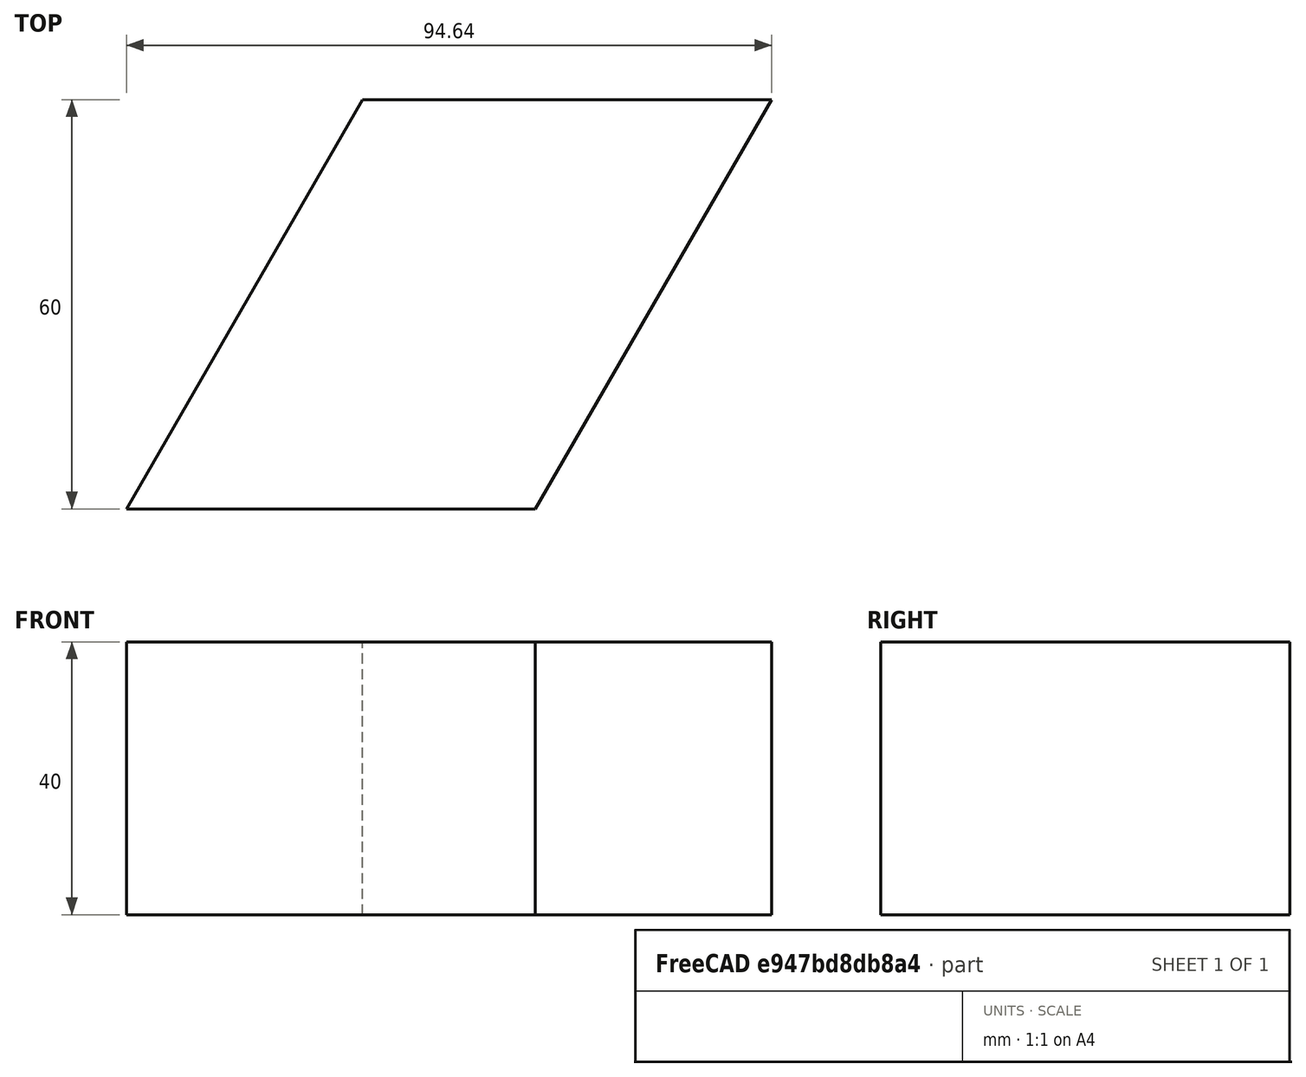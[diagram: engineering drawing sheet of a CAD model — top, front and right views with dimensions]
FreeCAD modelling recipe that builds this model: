
FCSTD DOCUMENT  (FreeCAD 0.19R)
Label: Rhombus
License: All rights reserved
LicenseURL: http://en.wikipedia.org/wiki/All_rights_reserved
objects: Sketcher::SketchObject×1, PartDesign::Pad×1, PartDesign::Body×1
note: 4 computed .brp shape members not serialized (recipe doc carries the construction recipe); baked Part::Feature solids carry a one-line shape summary decoded from their .brp

FEATURE [Sketcher::SketchObject] Sketch
  FullyConstrained = true
  MapMode = 5
  Support = -> [XY_Plane]
  sketch-geometry (4):
    g0: LineSegment StartX=57.631 StartY=83.67 StartZ=0 EndX=117.631 EndY=83.67 EndZ=0
    g1: LineSegment StartX=117.631 StartY=83.67 StartZ=0 EndX=82.99 EndY=23.67 EndZ=0
    g2: LineSegment StartX=82.99 StartY=23.67 StartZ=0 EndX=22.99 EndY=23.67 EndZ=0
    g3: LineSegment StartX=22.99 StartY=23.67 StartZ=0 EndX=57.631 EndY=83.67 EndZ=0
  constraints (12):
    c: Coincident(g0,g1)
    c: Coincident(g1,g2)
    c: Coincident(g2,g3)
    c: Coincident(g3,g0)
    c: Horizontal(g0)
    c: Horizontal(g2)
    c: DistanceX(g-1,g2) = 22.99
    c: DistanceY(g-1,g2) = 23.67
    c: DistanceX(g2,g1) = 60
    c: DistanceY(g1,g1) = 60
    c: Equal(g0,g2)
    c: Angle(g2,g3) = 1.0472
FEATURE [PartDesign::Pad] Pad
  Direction = (1,1,1)
  Length = 40
  Length2 = 100
  Profile = -> Sketch
  Type = 0
FEATURE [PartDesign::Body] Body
  Group = -> [Sketch,Pad]
  Origin = -> Origin
  Tip = -> Pad
